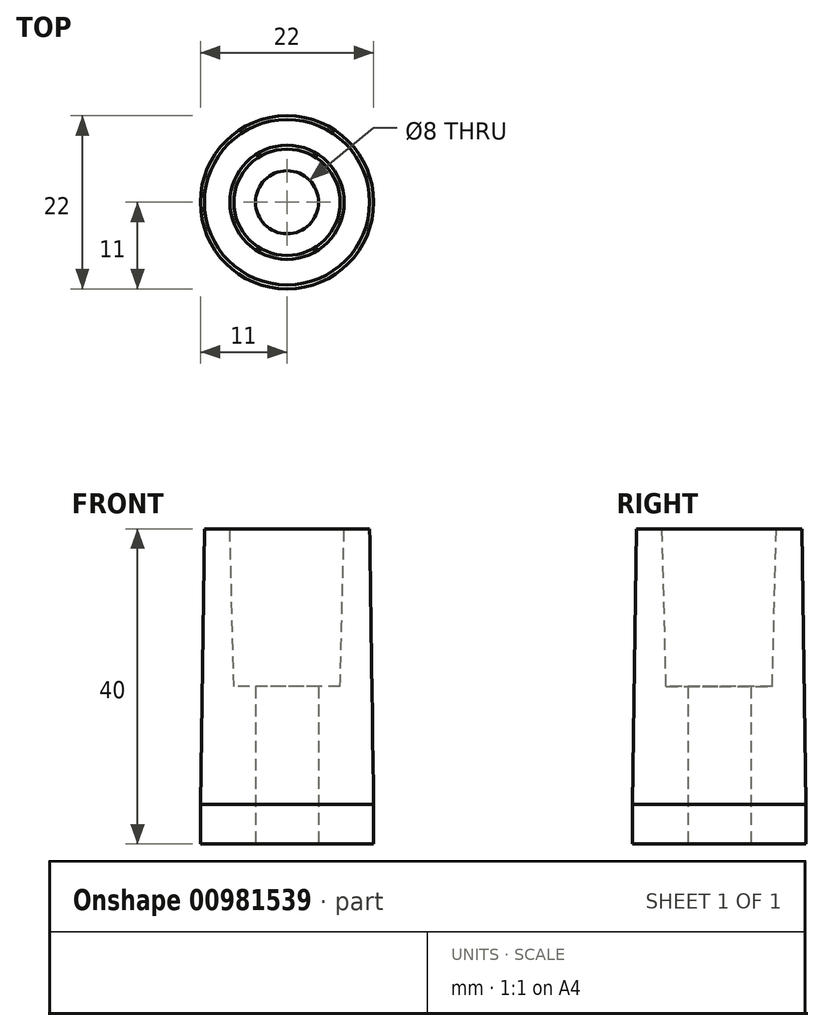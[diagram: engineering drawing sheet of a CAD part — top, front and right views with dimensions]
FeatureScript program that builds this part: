
annotation { "Feature Type Name" : "Feature", "Feature Type Description" : "" }
export const myFeature = defineFeature(function(context is Context, id is Id, definition is map)
    precondition{}
    {
        {
            var Q0;
            Q0=qCreatedBy(makeId("Top.planeOp"),FACE);
            var sketch = newSketch(context, id + "F0", { "sketchPlane" : qUnion([Q0])});
            skCircle(sketch, "E0", {"center": v(0, 0) * mm, "radius": 11 * mm});
            skCircle(sketch, "E1", {"center": v(0, 0) * mm, "radius": 6.75 * mm});
            skCircle(sketch, "E2", {"center": v(0, 0) * mm, "radius": 4 * mm});
            skSolve(sketch);
        }
        {
            var Q0;
            Q0=makeQuery(id+"F0.imprint","IMPRINT",FACE,{"disambiguationData":[TD([[makeQuery(id+"F0.imprint","IMPRINT",EDGE,{"derivedFrom":sQuery(id+"F0.wireOp",EDGE,"E0")}),1.0]])]});
            extrude(context, id + "F1", {"entities" : qUnion([Q0]), "depth" : 40 * mm, "offsetDistance" : 25 * mm});
        }
        {
            var Q0;
            Q0=makeQuery(id+"F0.imprint","IMPRINT",FACE,{"disambiguationData":[TD([[makeQuery(id+"F0.imprint","IMPRINT",EDGE,{"derivedFrom":sQuery(id+"F0.wireOp",EDGE,"E1")}),1.0]])]});
            extrude(context, id + "F2", {"entities" : qUnion([Q0]), "operationType" : NewBodyOperationType.ADD, "depth" : 20 * mm, "offsetDistance" : 25 * mm});
        }
        {
            var Q0;
            Q0=makeQuery(id+"F1.opExtrude","CAP_EDGE",EDGE,{"disambiguationData":[OSD([sQuery(id+"F0.wireOp",EDGE,"E1")])],"isStart":false});
            chamfer(context, id + "F3", {"entities" : qUnion([Q0]), "chamferType" : ChamferType.TWO_OFFSETS, "width1" : 0.5 * mm, "oppositeDirection" : true, "width2" : 20 * mm, "tangentPropagation" : true});
        }
        {
            var Q0;
            Q0=makeQuery(id+"F1.opExtrude","CAP_EDGE",EDGE,{"disambiguationData":[OSD([sQuery(id+"F0.wireOp",EDGE,"E0")])],"isStart":false});
            chamfer(context, id + "F4", {"entities" : qUnion([Q0]), "chamferType" : ChamferType.TWO_OFFSETS, "width1" : 0.5 * mm, "oppositeDirection" : false, "width2" : 35 * mm, "tangentPropagation" : true});
        }
    });
